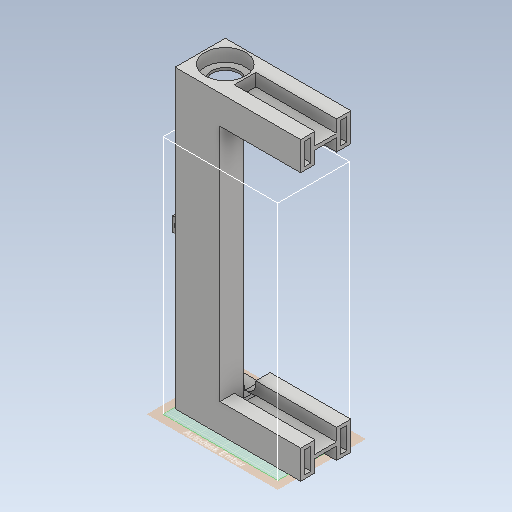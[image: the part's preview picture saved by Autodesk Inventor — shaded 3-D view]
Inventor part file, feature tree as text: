
AUTODESK INVENTOR PART (.ipt)
format: ipt  version: 2020 (Build 240168000, 168)  size: 608,768 bytes
history: native  units: mm
features: extrude x20, sketch x20, fillet x4
ambient origin geometry x8: Origin, YZ Plane, XZ Plane, XY Plane, X Axis, Y Axis, Z Axis, Center Point
bodies: Solid1 (feature_tree)
feature tree (44):
  extrude  "Extrusion1"  Depth=165.0mm
  extrude  "Extrusion2"  Depth=8.5mm
  extrude  "Extrusion3"  Depth=25.0mm TaperAngle=0.0deg
  extrude  "Extrusion4"  Depth=25.0mm
  extrude  "Extrusion5"  Depth=7.1mm
  extrude  "Extrusion6"  Depth=7.1mm TaperAngle=0.0deg
  fillet  "Fillet1"  Radius=5.0mm
  extrude  "Extrusion7"  Depth=10.0mm TaperAngle=0.0deg
  fillet  "Fillet2"  Radius=2.0mm
  extrude  "Extrusion8"  Depth=8.0mm
  extrude  "Extrusion9"  Depth=8.0mm
  fillet  "Fillet3"  Radius=8.0mm
  extrude  "Extrusion10"  Depth=6.0mm
  extrude  "Extrusion11"  Depth=3.5mm
  fillet  "Fillet4"  Radius=12.25mm
  extrude  "Extrusion12"  Depth=12.25mm
  extrude  "Extrusion13"  Depth=3.5mm
  extrude  "Extrusion14"  Depth=1.0mm
  sketch  "Sketch16"  dims[d40=2.0mm d41=8.0mm]
  extrude  "Extrusion15"  Depth=8.0mm
  extrude  "Extrusion16"  Depth=2.0mm
  extrude  "Extrusion17"  Depth=6.0mm
  extrude  "Extrusion18"  Depth=6.0mm
  extrude  "Extrusion19"  Depth=6.5mm TaperAngle=0.0deg
  extrude  "Extrusion20"  Depth=8.0mm TaperAngle=0.0deg
  sketch  "Sketch1"  dims[d0=25.0mm d1=165.0mm]
  sketch  "Sketch2"  dims[d2=3.0mm d3=0.0mm d4=8.5mm]
  sketch  "Sketch3"  dims[d5=8.5mm d6=25.0mm d7=0.0mm]
  sketch  "Sketch4"  dims[d8=25.0mm d9=22.75mm]
  sketch  "Sketch5"  dims[d10=7.1mm d11=0.0mm d12=15.5mm]
  sketch  "Sketch6"  dims[d13=165.0mm d14=0.0mm d15=7.1mm d16=0.0mm d17=5.0mm]
  sketch  "Sketch7"  dims[d18=5.0mm d19=10.0mm d20=0.0mm d21=2.0mm]
  sketch  "Sketch8"  dims[d22=16.0mm d23=8.0mm]
  sketch  "Sketch9"  dims[d24=16.0mm d25=16.0mm d26=8.0mm]
  sketch  "Sketch10"  dims[d27=45.0mm d28=0.0mm d29=6.0mm]
  sketch  "Sketch11"  dims[d30=12.25mm d31=3.5mm d32=12.25mm]
  sketch  "Sketch13"  dims[d33=3.5mm d34=12.25mm]
  sketch  "Sketch14"  dims[d35=12.25mm d36=3.5mm]
  sketch  "Sketch15"  dims[d37=40.0mm d38=0.0mm d39=1.0mm]
  sketch  "Sketch17"  dims[d42=1.0mm d43=2.0mm]
  sketch  "Sketch18"  dims[d44=12.0mm d45=0.0mm d46=6.0mm]
  sketch  "Sketch19"  dims[d47=6.0mm d48=4.0mm]
  sketch  "Sketch20"  dims[d49=8.0mm d50=6.5mm d51=0.0mm]
  sketch  "Sketch21"  dims[d52=6.35mm d53=8.0mm d54=0.0mm d55=6.5mm d56=47.0mm d57=1.0mm d58=7.0mm d59=0.0mm d60=7.1mm d61=0.0mm d62=14.5mm d63=0.0mm d64=2.0mm d65=0.0mm d66=8.5mm d67=2.0mm d68=0.0mm d69=20.0mm d70=0.0mm d71=165.0mm d72=0.0mm d73=47.0mm d74=0.0mm d75=6.0mm d76=148.0mm d77=0.0mm]
